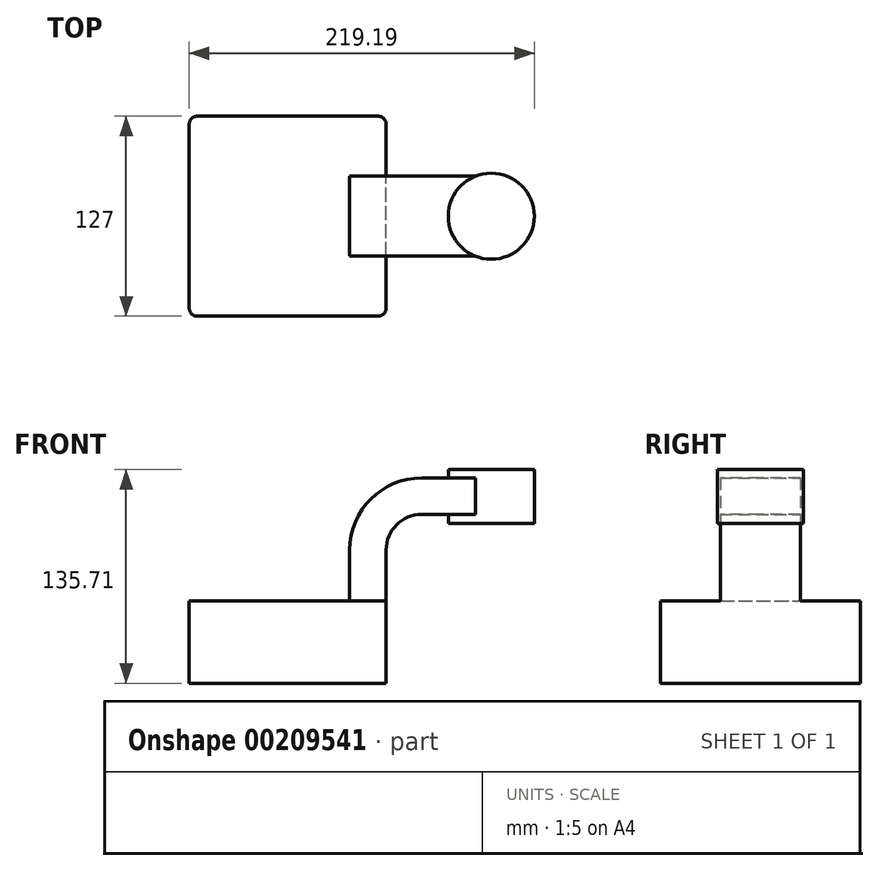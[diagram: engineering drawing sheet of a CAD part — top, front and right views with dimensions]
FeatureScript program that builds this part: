
annotation { "Feature Type Name" : "Feature", "Feature Type Description" : "" }
export const myFeature = defineFeature(function(context is Context, id is Id, definition is map)
    precondition{}
    {
        {
            var Q0;
            Q0=qCreatedBy(makeId("Front.planeOp"),FACE);
            var sketch = newSketch(context, id + "F0", { "sketchPlane" : qUnion([Q0])});
            skLineSegment(sketch, "E0.bottom", {"start": v(62.54, 26.16) * mm, "end": v(-62.54, 26.16) * mm});
            skLineSegment(sketch, "E0.top", {"start": v(62.54, -26.16) * mm, "end": v(-62.54, -26.16) * mm});
            skLineSegment(sketch, "E0.left", {"start": v(62.54, 26.16) * mm, "end": v(62.54, -26.16) * mm});
            skLineSegment(sketch, "E0.right", {"start": v(-62.54, 26.16) * mm, "end": v(-62.54, -26.16) * mm});
            skPoint(sketch, "E0.middle", {"position": v(0, 0) * mm});
            skLineSegment(sketch, "E1.bottom", {"start": v(156.65, 75.51) * mm, "end": v(102, 75.51) * mm});
            skLineSegment(sketch, "E1.top", {"start": v(156.65, 109.55) * mm, "end": v(102, 109.55) * mm});
            skLineSegment(sketch, "E1.left", {"start": v(156.65, 75.51) * mm, "end": v(156.65, 109.55) * mm});
            skLineSegment(sketch, "E1.right", {"start": v(102, 75.51) * mm, "end": v(102, 109.55) * mm});
            skPoint(sketch, "E1.middle", {"position": v(129.33, 92.53) * mm});
            skLineSegment(sketch, "E2", {"start": v(62.54, 26.16) * mm, "end": v(62.54, 58.54) * mm});
            skPoint(sketch, "E3.endSnap0", {"position": v(129.33, 75.51) * mm});
            skArc(sketch, "E4", {"start": v(62.54, 58.54) * mm, "mid": v(69.17, 74.54) * mm, "end": v(85.17, 81.17) * mm});
            skLineSegment(sketch, "E5", {"start": v(85.17, 81.17) * mm, "end": v(129.33, 81.17) * mm});
            skLineSegment(sketch, "E6.0", {"start": v(85.17, 104.28) * mm, "end": v(129.33, 104.28) * mm});
            skArc(sketch, "E6.1", {"start": v(39.42, 58.54) * mm, "mid": v(52.82, 90.88) * mm, "end": v(85.17, 104.28) * mm});
            skLineSegment(sketch, "E6.2", {"start": v(39.42, 26.16) * mm, "end": v(39.42, 58.54) * mm});
            skFitSpline(sketch, "E7", {"points": [v(-62.54, 26.16) * mm, v(85.17, 104.28) * mm], "startDerivative": vector(187.61, 0) * mm, "endDerivative": vector(162.34, 0) * mm});
            skLineSegment(sketch, "E8", {"start": v(129.33, 75.51) * mm, "end": v(129.33, 109.55) * mm});
            skSolve(sketch);
        }
        {
            var Q0;
            Q0=makeQuery(id+"F0.imprint","IMPRINT",FACE,{"disambiguationData":[TD([[makeQuery(id+"F0.imprint","IMPRINT",EDGE,{"derivedFrom":sQuery(id+"F0.wireOp",EDGE,"E0.top")}),-1.0]])]});
            extrude(context, id + "F1", {"entities" : qUnion([Q0]), "endBound" : BoundingType.SYMMETRIC, "depth" : 127 * mm});
        }
        {
            var Q0;
            {var subQ2=sQuery(id+"F0.wireOp",EDGE,"E2");Q0=makeQuery(id+"F0.imprint","IMPRINT",FACE,{"disambiguationData":[TD([[makeQuery(id+"F0.imprint","IMPRINT",EDGE,{"derivedFrom":subQ2}),1.0]])]});}
            extrude(context, id + "F2", {"entities" : qUnion([Q0]), "operationType" : NewBodyOperationType.ADD, "endBound" : BoundingType.SYMMETRIC, "depth" : 50.8 * mm});
        }
        {
            var Q0;
            Q0=makeQuery(id+"F0.imprint","IMPRINT",FACE,{"disambiguationData":[TD([[makeQuery(id+"F0.imprint","IMPRINT",EDGE,{"derivedFrom":sQuery(id+"F0.wireOp",EDGE,"E6.1")}),1.0]])]});
            extrude(context, id + "F3", {"entities" : qUnion([Q0]), "operationType" : NewBodyOperationType.ADD, "depth" : 25.4 * mm});
        }
        {
            var Q0;
            {var subQ0=sQuery(id+"F0.wireOp",EDGE,"E5");var subQ1=sQuery(id+"F0.wireOp",EDGE,"E1.right");var subQ2=makeQuery(id+"F0.imprint","INTERSECT",VERTEX,{"derivedFrom":[subQ1,subQ0]});Q0=makeQuery(id+"F0.imprint","IMPRINT",FACE,{"disambiguationData":[TD([[makeQuery(id+"F0.imprint","IMPRINT",EDGE,{"disambiguationData":[TD([[subQ2,-1.0]])],"derivedFrom":subQ1}),-1.0]])]});}
            extrude(context, id + "F4", {"entities" : qUnion([Q0]), "operationType" : NewBodyOperationType.ADD, "endBound" : BoundingType.SYMMETRIC, "depth" : 50.8 * mm});
        }
        {
            var Q0;
            {var subQ0=sQuery(id+"F0.wireOp",EDGE,"E1.left");Q0=makeQuery(id+"F0.imprint","IMPRINT",FACE,{"disambiguationData":[TD([[makeQuery(id+"F0.imprint","IMPRINT",EDGE,{"derivedFrom":subQ0}),1.0]])]});}
            var Q1;
            Q1=sQuery(id+"F0.wireOp",EDGE,"E8");
            revolve(context, id + "F5", {"operationType" : NewBodyOperationType.ADD, "entities" : qUnion([Q0]), "axis" : qUnion([Q1]), "revolveType" : RevolveType.FULL});
        }
        {
            var Q0;
            Q0=makeQuery(id+"F1.opExtrude","CAP_EDGE",EDGE,{"disambiguationData":[OSD([sQuery(id+"F0.wireOp",EDGE,"E0.left")])],"isStart":false});
            fillet(context, id + "F6", {"entities" : qUnion([Q0]), "radius" : 5.08 * mm, "tangentPropagation" : true, "allowEdgeOverflow" : false});
        }
        {
            var Q0;
            Q0=makeQuery(id+"F1.opExtrude","CAP_EDGE",EDGE,{"disambiguationData":[OSD([sQuery(id+"F0.wireOp",EDGE,"E0.right")])],"isStart":false});
            fillet(context, id + "F7", {"entities" : qUnion([Q0]), "radius" : 5.08 * mm, "tangentPropagation" : true, "allowEdgeOverflow" : false});
        }
        {
            var Q0;
            Q0=makeQuery(id+"F1.opExtrude","CAP_EDGE",EDGE,{"disambiguationData":[OSD([sQuery(id+"F0.wireOp",EDGE,"E0.right")])],"isStart":true});
            var Q1;
            Q1=makeQuery(id+"F1.opExtrude","CAP_EDGE",EDGE,{"disambiguationData":[OSD([sQuery(id+"F0.wireOp",EDGE,"E0.left")])],"isStart":true});
            fillet(context, id + "F8", {"entities" : qUnion([Q0, Q1]), "radius" : 5.08 * mm, "tangentPropagation" : true, "allowEdgeOverflow" : false});
        }
    });
